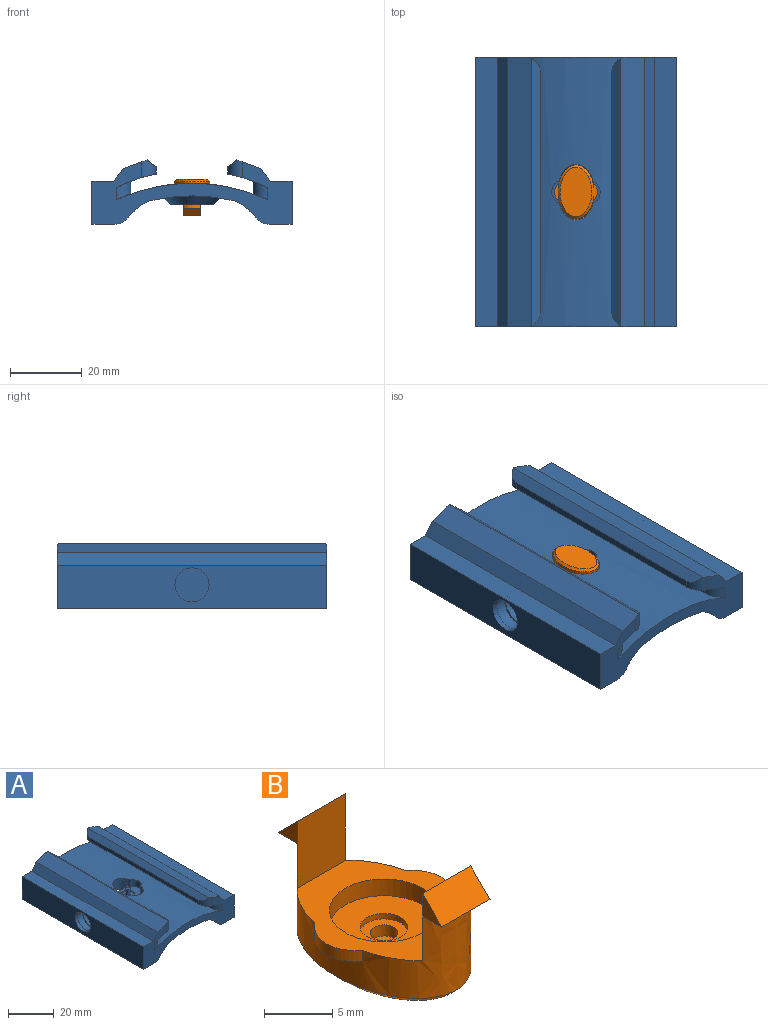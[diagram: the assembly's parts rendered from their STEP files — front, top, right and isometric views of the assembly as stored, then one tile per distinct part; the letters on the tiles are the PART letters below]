
ASSEMBLY  parts=2 mates=1
PART A: 63 faces, bbox 56.7x75.9x18.9 mm
  f0: extruded ~3.75x1.5mm, area 6mm2, adj f3,f53,f54,f58
  f1: extruded ~3.75x1.5mm, area 6mm2, adj f3,f52,f54,f57
  f2: plane 8.56x2mm, normal (0,-1,0), area 17.1mm2, adj f4,f53,f54
  f3: cylinder r=50.8mm len=75mm, axis (0,1,0), area 2473.8mm2, adj f0,f1,f21,f22,f30,f32,f44,f45
  f4: plane 19.16x12.16mm, normal (0,0,-1), area 138.2mm2, adj f2,f50,f51,f52,f53
  f5: cylinder r=5.25mm len=10.5mm, axis (-1,0,0), area 115.5mm2, adj f6,f10
  f6: plane 10.5x10.5mm, normal (-1,0,0), area 15.7mm2, adj f5,f8
  f7: plane 9.5x9.5mm, normal (-1,0,0), area 70.9mm2, adj f8
  f8: cylinder r=4.75mm len=9.5mm, axis (-1,0,0), area 119.4mm2, adj f6,f7
  f9: cylinder r=4.75mm len=9.5mm, axis (-1,0,0), area 44.8mm2, adj f10,f33
  f10: plane 10.5x10.5mm, normal (1,0,0), area 15.7mm2, adj f5,f9
  f11: cylinder r=50.91mm len=75mm, axis (0,1,0), area 1521.6mm2, adj f12,f28,f30,f32,f50
  f12: cylinder r=15mm len=75mm, axis (0,-1,0), area 563.3mm2, adj f11,f30,f32,f40
  f13: plane 75x6.36mm, normal (0,0,-1), area 476.7mm2, adj f14,f30,f32,f40
  f14: plane 75x12mm, normal (1,0,0), area 829.1mm2, adj f13,f15,f30,f32,f34
  f15: plane 75x6mm, normal (0,0,1), area 450mm2, adj f14,f16,f30,f32
  f16: plane 75x3.49mm, normal (0.78,0,0.63), area 337.5mm2, adj f15,f17,f30,f32
  f17: plane 75.01x6.55mm, normal (0.36,0,0.93), area 524.7mm2, adj f16,f18,f30,f32,f42,f46
  f18: plane 75.33x3.41mm, normal (-0.62,0,0.78), area 231.7mm2, adj f17,f19,f42,f46
  f19: plane 67x2mm, normal (-1,0,0), area 134mm2, adj f18,f20,f42,f46
  f20: cylinder r=39.16mm len=75mm, axis (0,1,0), area 547.9mm2, adj f19,f21,f30,f32,f42,f45,f46,f49
  f21: plane 67x3.5mm, normal (-1,0,0), area 234.5mm2, adj f3,f20,f45,f49
  f22: plane 67x3.5mm, normal (1,0,0), area 234.5mm2, adj f3,f23,f44,f48
  f23: cylinder r=39.16mm len=75mm, axis (0,1,0), area 547.9mm2, adj f22,f24,f30,f32,f43,f44,f47,f48
  f24: plane 67x2mm, normal (1,0,0), area 134mm2, adj f23,f25,f43,f47
  f25: plane 75.33x3.41mm, normal (0.62,0,0.78), area 231.7mm2, adj f24,f26,f43,f47
  f26: plane 75.01x6.55mm, normal (-0.36,0,0.93), area 524.7mm2, adj f25,f27,f30,f32,f43,f47
  f27: plane 75x3.49mm, normal (-0.78,0,0.63), area 337.5mm2, adj f26,f29,f30,f32
  f28: cylinder r=15mm len=75mm, axis (0,-1,0), area 563.3mm2, adj f11,f30,f32,f41
  f29: plane 75x6mm, normal (0,0,1), area 450mm2, adj f27,f30,f32,f33
  f30: plane 55.75x17.42mm, normal (0,-1,0), area 405mm2, adj f3,f11,f12,f13,f14,f15,f16,f17
  f31: plane 75x6.36mm, normal (0,0,-1), area 476.7mm2, adj f30,f32,f33,f41
  f32: plane 55.75x17.42mm, normal (0,1,0), area 405mm2, adj f3,f11,f12,f13,f14,f15,f16,f17
  f33: plane 75x12mm, normal (-1,0,0), area 829.1mm2, adj f9,f29,f30,f31,f32
  f34: cylinder r=4.75mm len=9.5mm, axis (1,0,0), area 44.8mm2, adj f14,f35
  f35: plane 10.5x10.5mm, normal (-1,0,0), area 15.7mm2, adj f34,f39
  f36: plane 9.5x9.5mm, normal (1,0,0), area 70.9mm2, adj f37
  f37: cylinder r=4.75mm len=9.5mm, axis (1,0,0), area 119.4mm2, adj f36,f38
  f38: plane 10.5x10.5mm, normal (1,0,0), area 15.7mm2, adj f37,f39
  f39: cylinder r=5.25mm len=10.5mm, axis (1,0,0), area 115.5mm2, adj f35,f38
  f40: cylinder r=4.65mm len=75mm, axis (0,-1,0), area 322.4mm2, adj f12,f13,f30,f32
  f41: cylinder r=4.65mm len=75mm, axis (0,-1,0), area 322.4mm2, adj f28,f30,f31,f32
  f42: cylinder r=4mm len=4.97mm, axis (0,0,-1), area 23mm2, adj f17,f18,f19,f20,f32
  f43: cylinder r=4mm len=4.97mm, axis (0,0,1), area 23mm2, adj f23,f24,f25,f26,f32
  f44: cylinder r=4mm len=5.11mm, axis (0,0,1), area 21.3mm2, adj f3,f22,f23,f32
  f45: cylinder r=4mm len=5.11mm, axis (0,0,-1), area 21.3mm2, adj f3,f20,f21,f32
  f46: cylinder r=4mm len=4.97mm, axis (0,0,1), area 23mm2, adj f17,f18,f19,f20,f30
  f47: cylinder r=4mm len=4.97mm, axis (0,0,-1), area 23mm2, adj f23,f24,f25,f26,f30
  f48: cylinder r=4mm len=5.11mm, axis (0,0,-1), area 21.3mm2, adj f3,f22,f23,f30
  f49: cylinder r=4mm len=5.11mm, axis (0,0,1), area 21.3mm2, adj f3,f20,f21,f30
  f50: bspline ~25x18mm, area 195mm2, adj f4,f11
  f51: plane 8.54x2mm, normal (0,1,0), area 17.1mm2, adj f4,f52,f54
  f52: extruded ~8.54x5.75mm, area 65mm2, adj f1,f3,f4,f51,f55
  f53: extruded ~8.56x5.75mm, area 65.2mm2, adj f0,f2,f3,f4,f56
  f54: plane 13.5x9.01mm, normal (0,0,1), area 73.8mm2, adj f0,f1,f2,f51,f55,f56,f57,f58
  f55: extruded ~3.75x1.5mm, area 6mm2, adj f3,f52,f54,f58
  f56: extruded ~3.75x1.5mm, area 6mm2, adj f3,f53,f54,f57
  f57: cylinder r=3.31mm len=6mm, axis (0,0,-1), area 27.8mm2, adj f1,f3,f54,f56
  f58: cylinder r=3.31mm len=6mm, axis (0,0,-1), area 27.8mm2, adj f0,f3,f54,f55
  f59: cylinder r=3mm len=6mm, axis (0,0,1), area 9.4mm2, adj f54,f60
  f60: plane 6x6mm, normal (0,0,1), area 25.1mm2, adj f59,f62
  f61: plane 2x2mm, normal (0,0,1), area 3.1mm2, adj f62
  f62: cylinder r=1mm len=3.5mm, axis (0,0,-1), area 22mm2, adj f60,f61
PART B: 24 faces, bbox 12.1x17.1x10.1 mm
  f0: cylinder r=1.75mm len=3.5mm, axis (0,0,1), area 5.5mm2, adj f1,f5
  f1: plane 3.5x3.5mm, normal (0,0,1), area 6.5mm2, adj f0,f3
  f2: plane 2x2mm, normal (0,0,1), area 3.1mm2, adj f3
  f3: cylinder r=1mm len=2mm, axis (0,0,1), area 6.3mm2, adj f1,f2
  f4: cylinder r=4mm len=8mm, axis (0,0,1), area 37.7mm2, adj f5,f22
  f5: plane 8x8mm, normal (0,0,1), area 40.6mm2, adj f0,f4
  f6: plane 4.99x2mm, normal (0,0.71,0.71), area 14.1mm2, adj f7,f8,f13,f18
  f7: plane 2x2mm, normal (1,0,0), area 2mm2, adj f6,f13,f18
  f8: plane 2x2mm, normal (-1,0,0), area 2mm2, adj f6,f13,f18
  f9: plane 2x2mm, normal (1,0,0), area 2mm2, adj f10,f15,f20
  f10: plane 4.99x2mm, normal (0,-0.71,0.71), area 14.1mm2, adj f9,f11,f15,f20
  f11: plane 2x2mm, normal (-1,0,0), area 2mm2, adj f10,f15,f20
  f12: plane 4.94x1.28mm, normal (0,0,-1), area 3.4mm2, adj f19,f21
  f13: plane 4.99x2mm, normal (0,0,-1), area 6.6mm2, adj f6,f7,f8,f21
  f14: plane 4.94x1.28mm, normal (0,0,-1), area 3.4mm2, adj f17,f21
  f15: plane 4.99x2mm, normal (0,0,-1), area 6.6mm2, adj f9,f10,f11,f21
  f16: plane 13.9x8.89mm, normal (0,0,-1), area 94.8mm2, adj f23
  f17: extruded ~4.94x1.28mm, area 5.7mm2, adj f14,f21,f22
  f18: plane 6x4.99mm, normal (0,-1,0), area 29.9mm2, adj f6,f7,f8,f21,f22
  f19: extruded ~4.94x1.28mm, area 5.7mm2, adj f12,f21,f22
  f20: plane 6x4.99mm, normal (0,1,0), area 29.9mm2, adj f9,f10,f11,f21,f22
  f21: extruded ~15x10mm, area 168.8mm2, adj f12,f13,f14,f15,f17,f18,f19,f20
  f22: plane 13x12mm, normal (0,0,1), area 67.6mm2, adj f4,f17,f18,f19,f20,f21
  f23: bspline ~14.97x10mm, area 32.1mm2, adj f16,f21
PLACE A t=(-0.01,37.39,0.85)mm
PLACE B rot(axis=(1,0,0),180deg) t=(-0.01,-0.12,2.85)mm
MATE fastened B.f0 <-> A.f59  axis (0,0,-1) through (-0.01,-0.12,0.85)mm
